# Revit family: IS_ConnectAir_A7030_BIM_FR
name_source: partatom
category: Plumbing Fixtures
revit_build: Autodesk Revit 2017 (Build: 20160225_1515(x64)
units: mm (PartAtom-declared; Revit-internal decimal feet)

## family parameters
Always vertical = No
Cut with Voids When Loaded = No
OmniClass Number = 23.45.55.17
OmniClass Title = Mixing Faucets
Part Type = Normal
Room Calculation Point = No
Round Connector Dimension = Use Diameter
Shared = No
Work Plane-Based = No

## types (1)
- A7030AA - Connect Air Bid Mixer  Slim Pu/M
    Accessoires = www.idealstandard.be
    Auteur = Ideal Standard
    BOSUseNativeGeometries = 1
    Bim-NomDuProjet = ISI_IdealStandard_
    Caractéristiques = CONNECTEUR MECANICASSE D'AIR CONNECT RMTD SLM PU / M
    CodeBarre = 4015413342070
    ConseilsDInstallation = www.idealstandard.be
    Cost = 0 $
    Couleur = Chrome
    CoûtDeRemplacement = 0
    DateDeCréation = 2018_08_15
    Description = CONNECTEUR MECANICASSE D'AIR CONNECT RMTD SLM PU / M
    Dimensions = 48 x 153 x 147 mm
    Espace = Interne
    Finition = Chrome
    Forme = Complexe
    Hauteur = 147 mm
    IfcExportAs = IfcValveType
    IfcExportType = FAUCET
    InformationsProduit = www.idealstandard.be
    Largeur = 48 mm  [stored 0.15748 ft]
    LienUtile = www.idealstandard.be
    Longueur = 153 mm
    Manufacturer = www.idealstandard.be
    Marque = Ideal Standard
    Model = A7030AA
    PoidsNet = 1,43 KG
    PressionDeFonctionnement = 0
    PressionMaximum = 3 Bar
    Profondeur = 0 mm  [stored 0 ft]
    Raccordement = Plomberie
    Révision = 1
    TypeDeRobinetterie = Raccords d'alimentation en eau de bidet
    URL = www.idealstandard.be
    Uniclass2015Code = PR-35-06-10
    Uniclass2015Title = Bidet Water Supply Fittings
    Uniclass2015Version = Products v1.1
    UnitéDeMesure = Millimètres
    UnitéDeTemps = An
    UnitéMonétaire = €
    UrlDuFabricant = www.idealstandard.be
    UsageDeLaRobinetterie = Raccords d'alimentation en eau de bidet
    Version = 1

note: [stored X ft] marks values corroborated as IEEE doubles in the binary element streams (Revit-internal decimal feet)

## geometry (parser evidence)
native form markers: Sweep x2
no freeform markers — native parametric forms only
